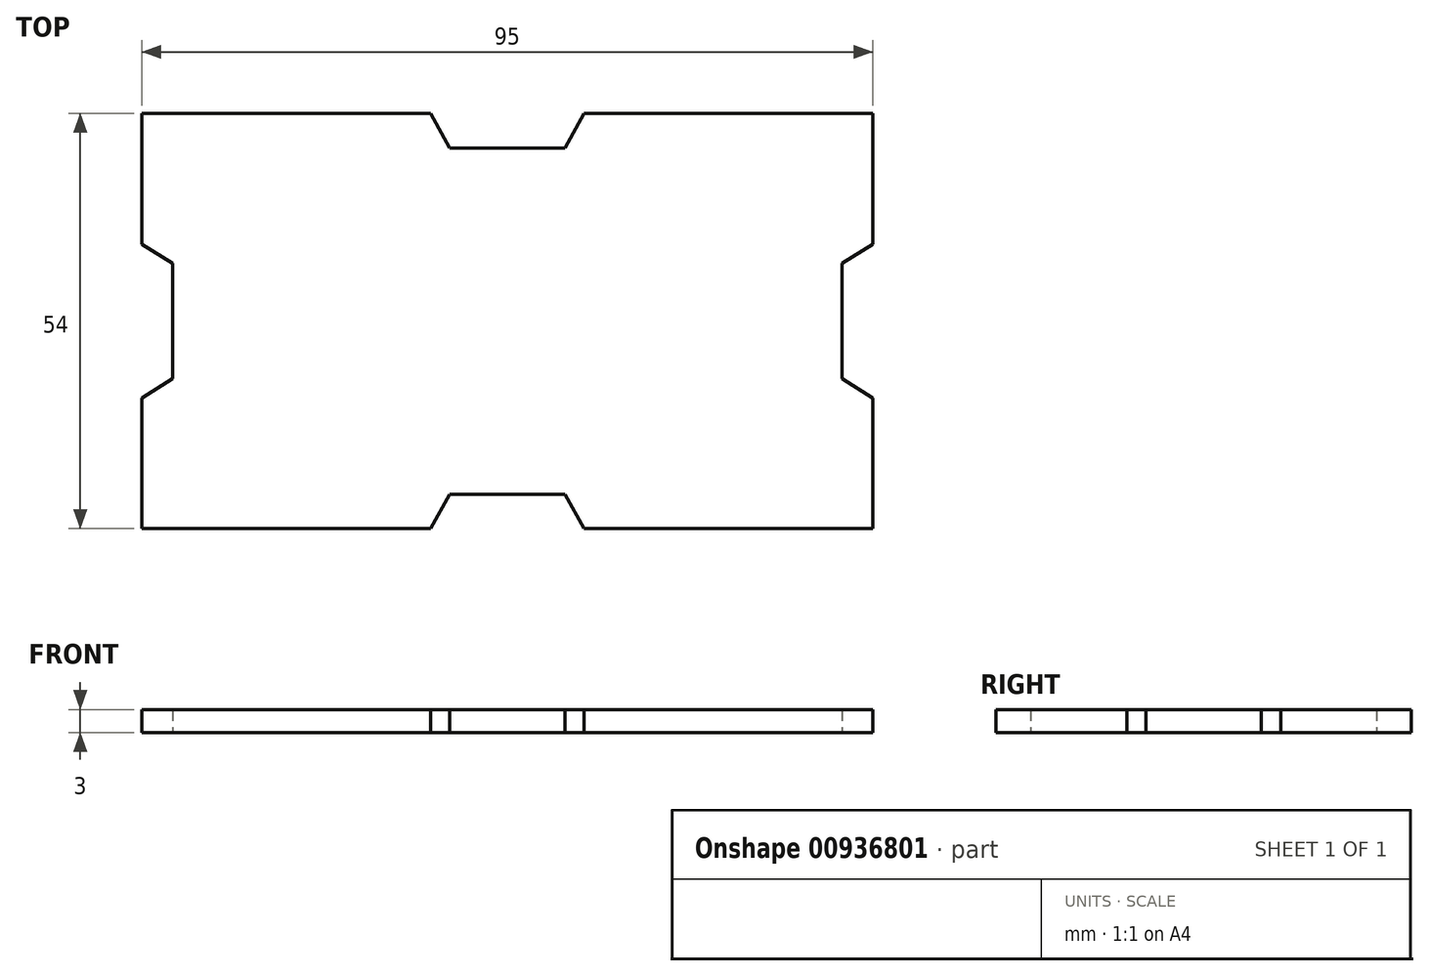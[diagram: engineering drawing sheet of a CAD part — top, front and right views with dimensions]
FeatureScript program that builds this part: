
annotation { "Feature Type Name" : "Feature", "Feature Type Description" : "" }
export const myFeature = defineFeature(function(context is Context, id is Id, definition is map)
    precondition{}
    {
        {
            var Q0;
            Q0=qCreatedBy(makeId("Top.planeOp"),FACE);
            var sketch = newSketch(context, id + "F0", { "sketchPlane" : qUnion([Q0])});
            skLineSegment(sketch, "E0", {"start": v(0, 54) * mm, "end": v(37.5, 54) * mm});
            skLineSegment(sketch, "E1", {"start": v(47.5, 4.5) * mm, "end": v(40, 4.5) * mm});
            skLineSegment(sketch, "E2", {"start": v(40, 4.5) * mm, "end": v(37.5, 0) * mm});
            skLineSegment(sketch, "E3", {"start": v(47.5, 4.5) * mm, "end": v(55, 4.5) * mm});
            skLineSegment(sketch, "E4", {"start": v(55, 4.5) * mm, "end": v(57.5, 0) * mm});
            skLineSegment(sketch, "E5", {"start": v(47.5, 49.5) * mm, "end": v(55, 49.5) * mm});
            skLineSegment(sketch, "E6", {"start": v(55, 49.5) * mm, "end": v(57.5, 54) * mm});
            skLineSegment(sketch, "E7", {"start": v(47.5, 49.5) * mm, "end": v(40, 49.5) * mm});
            skLineSegment(sketch, "E8", {"start": v(40, 49.5) * mm, "end": v(37.5, 54) * mm});
            skLineSegment(sketch, "E9.trimOffspring", {"start": v(57.5, 54) * mm, "end": v(95, 54) * mm});
            skLineSegment(sketch, "E10", {"start": v(37.5, 0) * mm, "end": v(0, 0) * mm});
            skLineSegment(sketch, "E11", {"start": v(57.5, 0) * mm, "end": v(95, 0) * mm});
            skLineSegment(sketch, "E12", {"start": v(4, 27) * mm, "end": v(4, 34.5) * mm});
            skLineSegment(sketch, "E13", {"start": v(4, 34.5) * mm, "end": v(0, 37) * mm});
            skLineSegment(sketch, "E14", {"start": v(4, 27) * mm, "end": v(4, 19.5) * mm});
            skLineSegment(sketch, "E15", {"start": v(4, 19.5) * mm, "end": v(0, 17) * mm});
            skLineSegment(sketch, "E16", {"start": v(91, 27) * mm, "end": v(91, 19.5) * mm});
            skLineSegment(sketch, "E17", {"start": v(91, 27) * mm, "end": v(91, 34.5) * mm});
            skLineSegment(sketch, "E18", {"start": v(95, 17) * mm, "end": v(91, 19.5) * mm});
            skLineSegment(sketch, "E19", {"start": v(91, 34.5) * mm, "end": v(95, 37) * mm});
            skLineSegment(sketch, "E20", {"start": v(37.5, 54) * mm, "end": v(37.5, 0) * mm});
            skLineSegment(sketch, "E21", {"start": v(0, 37) * mm, "end": v(0, 17) * mm});
            skLineSegment(sketch, "E22", {"start": v(95, 37) * mm, "end": v(95, 17) * mm});
            skLineSegment(sketch, "E23", {"start": v(0, 54) * mm, "end": v(0, 37) * mm});
            skLineSegment(sketch, "E24", {"start": v(0, 17) * mm, "end": v(0, 0) * mm});
            skLineSegment(sketch, "E25", {"start": v(95, 17) * mm, "end": v(95, 0) * mm});
            skLineSegment(sketch, "E26", {"start": v(95, 37) * mm, "end": v(95, 54) * mm});
            skLineSegment(sketch, "E27", {"start": v(0, 37) * mm, "end": v(95, 37) * mm});
            skSolve(sketch);
        }
        {
            var Q0;
            Q0=makeQuery(id+"F0.imprint","IMPRINT",FACE,{"disambiguationData":[TD([[makeQuery(id+"F0.imprint","IMPRINT",EDGE,{"derivedFrom":sQuery(id+"F0.wireOp",EDGE,"LtiW4xSU-nM4P-1xAS-1kRZ-mRGgfVFdoBoQ")}),-1.0]])]});
            var Q1;
            Q1=makeQuery(id+"F0.imprint","IMPRINT",FACE,{"disambiguationData":[TD([[makeQuery(id+"F0.imprint","IMPRINT",EDGE,{"derivedFrom":sQuery(id+"F0.wireOp",EDGE,"fYObT11j-cXBY-Dhv8-buVp-M8uKFhghbAF0")}),-1.0]])]});
            var Q2;
            Q2=makeQuery(id+"F0.imprint","IMPRINT",FACE,{"disambiguationData":[TD([[makeQuery(id+"F0.imprint","IMPRINT",EDGE,{"derivedFrom":sQuery(id+"F0.wireOp",EDGE,"E0")}),-1.0]])]});
            var Q3;
            Q3=makeQuery(id+"F0.imprint","IMPRINT",FACE,{"disambiguationData":[TD([[makeQuery(id+"F0.imprint","IMPRINT",EDGE,{"derivedFrom":sQuery(id+"F0.wireOp",EDGE,"E1")}),-1.0]])]});
            var Q4;
            Q4=makeQuery(id+"F0.imprint","IMPRINT",FACE,{"disambiguationData":[TD([[makeQuery(id+"F0.imprint","IMPRINT",EDGE,{"derivedFrom":sQuery(id+"F0.wireOp",EDGE,"E5")}),-1.0]])]});
            var Q5;
            {var subQ1=sQuery(id+"F0.wireOp",EDGE,"E10");Q5=makeQuery(id+"F0.imprint","IMPRINT",FACE,{"disambiguationData":[TD([[makeQuery(id+"F0.imprint","IMPRINT",EDGE,{"derivedFrom":subQ1}),-1.0]])]});}
            extrude(context, id + "F1", {"entities" : qUnion([Q0, Q1, Q2, Q3, Q4, Q5]), "depth" : 3 * mm, "offsetDistance" : 25 * mm});
        }
    });
